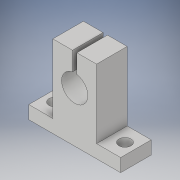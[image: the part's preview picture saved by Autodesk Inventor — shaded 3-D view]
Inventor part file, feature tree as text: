
AUTODESK INVENTOR PART (.ipt)
format: ipt  version: 2019 (Build 230136000, 136)  size: 131,072 bytes
history: native  units: mm
features: extrude x2, sketch x2
ambient origin geometry x8: Origin, YZ Plane, XZ Plane, XY Plane, X Axis, Y Axis, Z Axis, Center Point
bodies: Solid1 (feature_tree)
feature tree (4):
  extrude  "Extrusion1"  Depth=23.0mm
  extrude  "Extrusion2"  Depth=14.0mm
  sketch  "Sketch1"  dims[d0=12.0mm d1=23.0mm]
  sketch  "Sketch2"  dims[d2=42.0mm d3=21.0mm d4=6.0mm d7=9.0mm d8=9.0mm d10=37.5mm d11=37.5mm d14=10.0mm d15=31.5mm d16=6.0mm d17=10.0mm d18=14.0mm d19=0.0mm d20=5.5mm d21=5.5mm d22=32.0mm d23=16.0mm d24=7.0mm d25=16.0mm d26=14.0mm d27=0.0mm]
